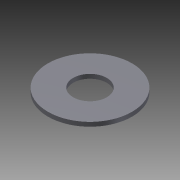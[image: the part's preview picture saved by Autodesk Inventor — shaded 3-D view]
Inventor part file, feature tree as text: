
AUTODESK INVENTOR PART (.ipt)
format: ipt  version: 2012 (Build 160160000, 160)  size: 71,680 bytes
history: native  units: mm
features: extrude x1, sketch x1
ambient origin geometry x8: Origin, YZ Plane, XZ Plane, XY Plane, X Axis, Y Axis, Z Axis, Center Point
bodies: Solid1 (feature_tree)
feature tree (2):
  extrude  "Extrusion1"  Depth=20.0mm
  sketch  "Sketch1"  dims[d0=8.0mm d1=20.0mm d2=1.0mm d3=0.0mm]
